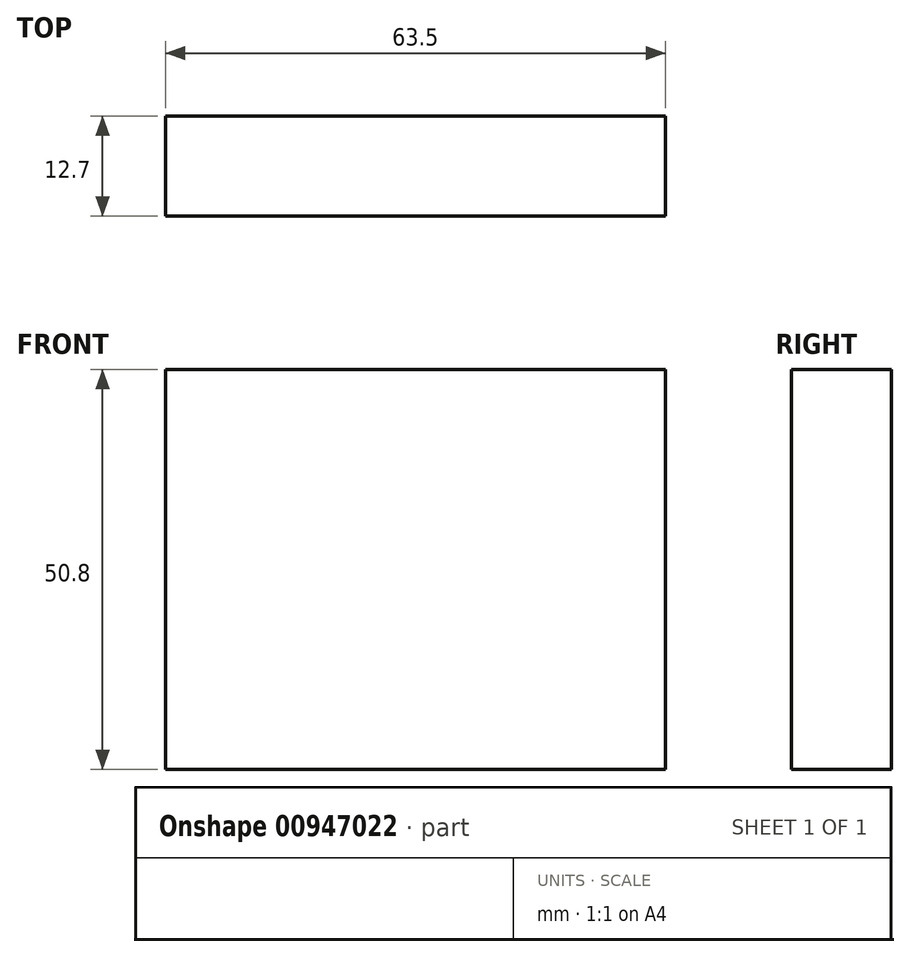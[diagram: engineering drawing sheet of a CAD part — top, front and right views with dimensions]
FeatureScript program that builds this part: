
annotation { "Feature Type Name" : "Feature", "Feature Type Description" : "" }
export const myFeature = defineFeature(function(context is Context, id is Id, definition is map)
    precondition{}
    {
        {
            var Q0;
            Q0=qCreatedBy(makeId("Front.planeOp"),FACE);
            var sketch = newSketch(context, id + "F0", { "sketchPlane" : qUnion([Q0])});
            skLineSegment(sketch, "E0.bottom", {"start": v(0, 0) * mm, "end": v(63.5, 0) * mm});
            skLineSegment(sketch, "E0.top", {"start": v(0, 50.8) * mm, "end": v(63.5, 50.8) * mm});
            skLineSegment(sketch, "E0.left", {"start": v(0, 0) * mm, "end": v(0, 50.8) * mm});
            skLineSegment(sketch, "E0.right", {"start": v(63.5, 0) * mm, "end": v(63.5, 50.8) * mm});
            skSolve(sketch);
        }
        {
            var Q0;
            Q0=makeQuery(id+"F0.imprint","IMPRINT",FACE,{"disambiguationData":[TD([[makeQuery(id+"F0.imprint","IMPRINT",EDGE,{"derivedFrom":sQuery(id+"F0.wireOp",EDGE,"E0.bottom")}),1.0]])]});
            extrude(context, id + "F1", {"entities" : qUnion([Q0]), "depth" : 12.7 * mm, "offsetDistance" : 25.4 * mm});
        }
    });
